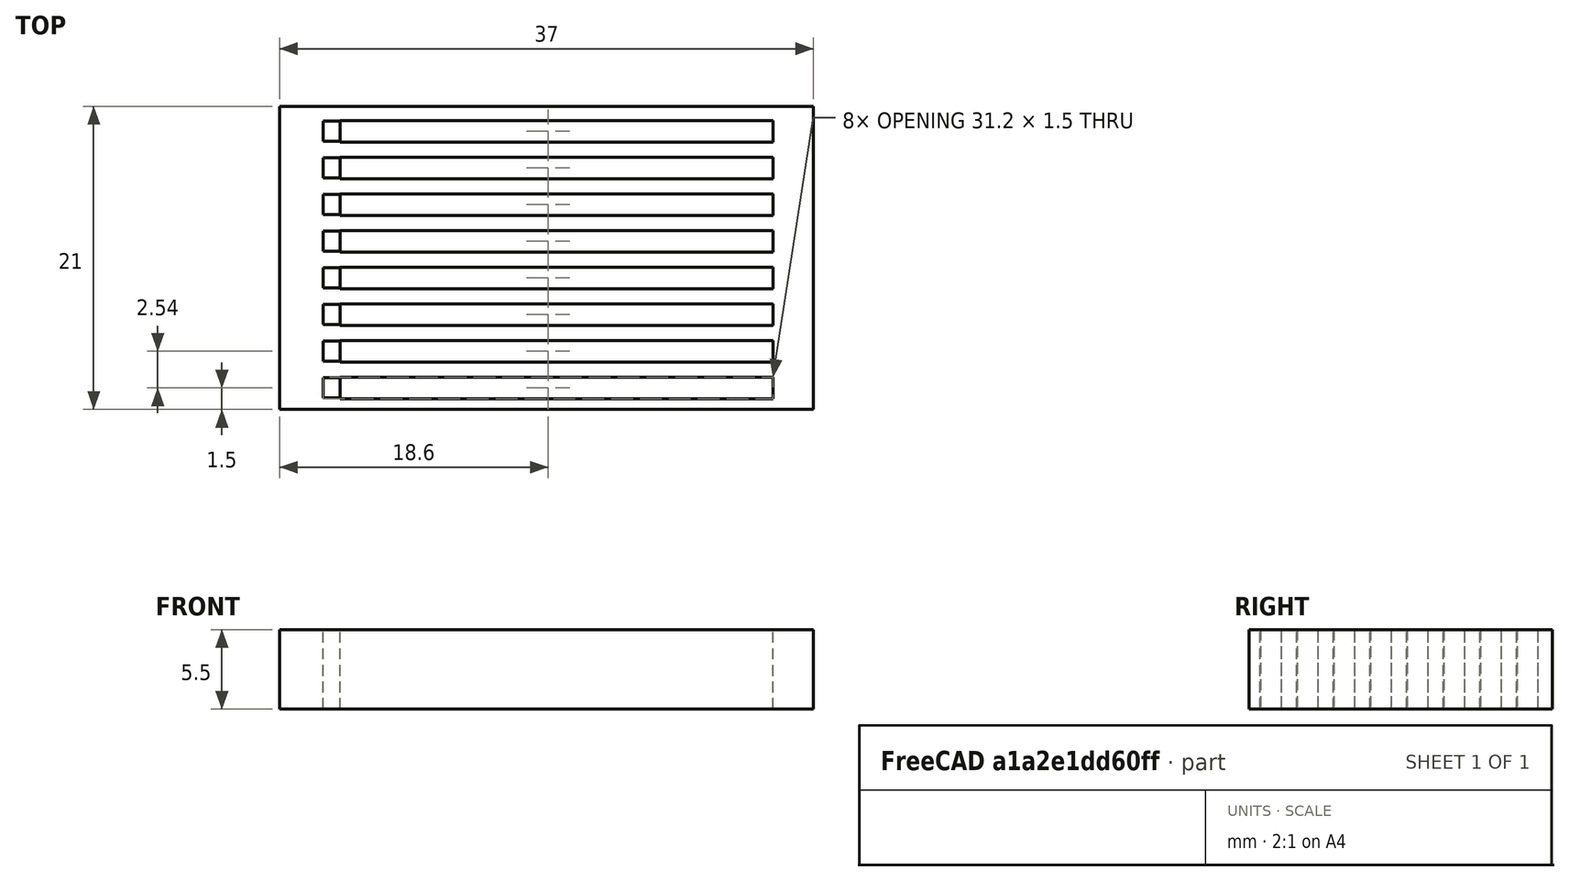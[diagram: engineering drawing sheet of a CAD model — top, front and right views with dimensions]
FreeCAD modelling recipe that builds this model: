
FCSTD DOCUMENT  (FreeCAD 0.17R13522 (Git))
Label: Test Piece V3 1.2
License: All rights reserved
LicenseURL: http://en.wikipedia.org/wiki/All_rights_reserved
objects: Part::Box×25, Part::MultiFuse×3, Part::Cut×2
note: 30 computed .brp shape members not serialized (recipe doc carries the construction recipe); baked Part::Feature solids carry a one-line shape summary decoded from their .brp

FEATURE [Part::Box] Box  label="Cube"
  AttacherType = Attacher::AttachEngine3D
  Height = 5.5
  Length = 37
  Width = 21
FEATURE [Part::Box] Box001  label="Cube001"
  AttacherType = Attacher::AttachEngine3D
  Height = 10
  Length = 1.6
  Placement = pos=(3,0.8,-3) rot=(0,0,1;0rad)
  Width = 1.4
FEATURE [Part::Box] Box002  label="Cube002"
  AttacherType = Attacher::AttachEngine3D
  Height = 10
  Length = 1.6
  Placement = pos=(3,3.34,-3) rot=(0,0,1;0rad)
  Width = 1.4
FEATURE [Part::Box] Box003  label="Cube003"
  AttacherType = Attacher::AttachEngine3D
  Height = 10
  Length = 1.6
  Placement = pos=(3,5.88,-3) rot=(0,0,1;0rad)
  Width = 1.4
FEATURE [Part::Box] Box004  label="Cube004"
  AttacherType = Attacher::AttachEngine3D
  Height = 10
  Length = 1.6
  Placement = pos=(3,8.42,-3) rot=(0,0,1;0rad)
  Width = 1.4
FEATURE [Part::Box] Box005  label="Cube005"
  AttacherType = Attacher::AttachEngine3D
  Height = 10
  Length = 1.6
  Placement = pos=(3,10.96,-3) rot=(0,0,1;0rad)
  Width = 1.4
FEATURE [Part::Box] Box006  label="Cube006"
  AttacherType = Attacher::AttachEngine3D
  Height = 10
  Length = 1.6
  Placement = pos=(3,13.5,-3) rot=(0,0,1;0rad)
  Width = 1.4
FEATURE [Part::Box] Box007  label="Cube007"
  AttacherType = Attacher::AttachEngine3D
  Height = 10
  Length = 1.6
  Placement = pos=(3,16.04,-3) rot=(0,0,1;0rad)
  Width = 1.4
FEATURE [Part::Box] Box008  label="Cube008"
  AttacherType = Attacher::AttachEngine3D
  Height = 10
  Length = 1.6
  Placement = pos=(3,18.58,-3) rot=(0,0,1;0rad)
  Width = 1.4
FEATURE [Part::Box] Box009  label="Cube009"
  AttacherType = Attacher::AttachEngine3D
  Height = 5.5
  Length = 30
  Placement = pos=(4.2,0.75,0) rot=(0,0,1;0rad)
  Width = 1.5
FEATURE [Part::Box] Box010  label="Cube010"
  AttacherType = Attacher::AttachEngine3D
  Height = 5.5
  Length = 30
  Placement = pos=(4.2,3.29,0) rot=(0,0,1;0rad)
  Width = 1.5
FEATURE [Part::Box] Box011  label="Cube011"
  AttacherType = Attacher::AttachEngine3D
  Height = 5.5
  Length = 30
  Placement = pos=(4.2,5.83,0) rot=(0,0,1;0rad)
  Width = 1.5
FEATURE [Part::Box] Box012  label="Cube012"
  AttacherType = Attacher::AttachEngine3D
  Height = 5.5
  Length = 30
  Placement = pos=(4.2,8.37,0) rot=(0,0,1;0rad)
  Width = 1.5
FEATURE [Part::Box] Box013  label="Cube013"
  AttacherType = Attacher::AttachEngine3D
  Height = 5.5
  Length = 30
  Placement = pos=(4.2,10.91,0) rot=(0,0,1;0rad)
  Width = 1.5
FEATURE [Part::Box] Box014  label="Cube014"
  AttacherType = Attacher::AttachEngine3D
  Height = 5.5
  Length = 30
  Placement = pos=(4.2,13.45,0) rot=(0,0,1;0rad)
  Width = 1.5
FEATURE [Part::Box] Box015  label="Cube015"
  AttacherType = Attacher::AttachEngine3D
  Height = 5.5
  Length = 30
  Placement = pos=(4.2,15.99,0) rot=(0,0,1;0rad)
  Width = 1.5
FEATURE [Part::Box] Box016  label="Cube016"
  AttacherType = Attacher::AttachEngine3D
  Height = 5.5
  Length = 30
  Placement = pos=(4.2,18.53,0) rot=(0,0,1;0rad)
  Width = 1.5
FEATURE [Part::MultiFuse] Fusion  label="Conducting Filament"
  Shapes = -> [Box009,Box010,Box011,Box012,Box013,Box014,Box015,Box016]
FEATURE [Part::MultiFuse] Fusion001
  Shapes = -> [Box001,Box002,Box003,Box004,Box005,Box006,Box007,Box008]
FEATURE [Part::Cut] Cut
  Base = -> Box
  Tool = -> Fusion001
FEATURE [Part::Box] Box017  label="Cube017"
  AttacherType = Attacher::AttachEngine3D
  Height = 5.5
  Length = 30
  Placement = pos=(4.2,0.75,0) rot=(0,0,1;0rad)
  Width = 1.5
FEATURE [Part::Box] Box018  label="Cube018"
  AttacherType = Attacher::AttachEngine3D
  Height = 5.5
  Length = 30
  Placement = pos=(4.2,10.91,0) rot=(0,0,1;0rad)
  Width = 1.5
FEATURE [Part::Box] Box019  label="Cube019"
  AttacherType = Attacher::AttachEngine3D
  Height = 5.5
  Length = 30
  Placement = pos=(4.2,3.29,0) rot=(0,0,1;0rad)
  Width = 1.5
FEATURE [Part::Box] Box020  label="Cube020"
  AttacherType = Attacher::AttachEngine3D
  Height = 5.5
  Length = 30
  Placement = pos=(4.2,5.83,0) rot=(0,0,1;0rad)
  Width = 1.5
FEATURE [Part::Box] Box021  label="Cube021"
  AttacherType = Attacher::AttachEngine3D
  Height = 5.5
  Length = 30
  Placement = pos=(4.2,18.53,0) rot=(0,0,1;0rad)
  Width = 1.5
FEATURE [Part::Box] Box022  label="Cube022"
  AttacherType = Attacher::AttachEngine3D
  Height = 5.5
  Length = 30
  Placement = pos=(4.2,15.99,0) rot=(0,0,1;0rad)
  Width = 1.5
FEATURE [Part::Box] Box023  label="Cube023"
  AttacherType = Attacher::AttachEngine3D
  Height = 5.5
  Length = 30
  Placement = pos=(4.2,8.37,0) rot=(0,0,1;0rad)
  Width = 1.5
FEATURE [Part::Box] Box024  label="Cube024"
  AttacherType = Attacher::AttachEngine3D
  Height = 5.5
  Length = 30
  Placement = pos=(4.2,13.45,0) rot=(0,0,1;0rad)
  Width = 1.5
FEATURE [Part::MultiFuse] Fusion002
  Shapes = -> [Box017,Box018,Box019,Box020,Box021,Box022,Box023,Box024]
FEATURE [Part::Cut] Cut001  label="Main body"
  Base = -> Cut
  Tool = -> Fusion002
